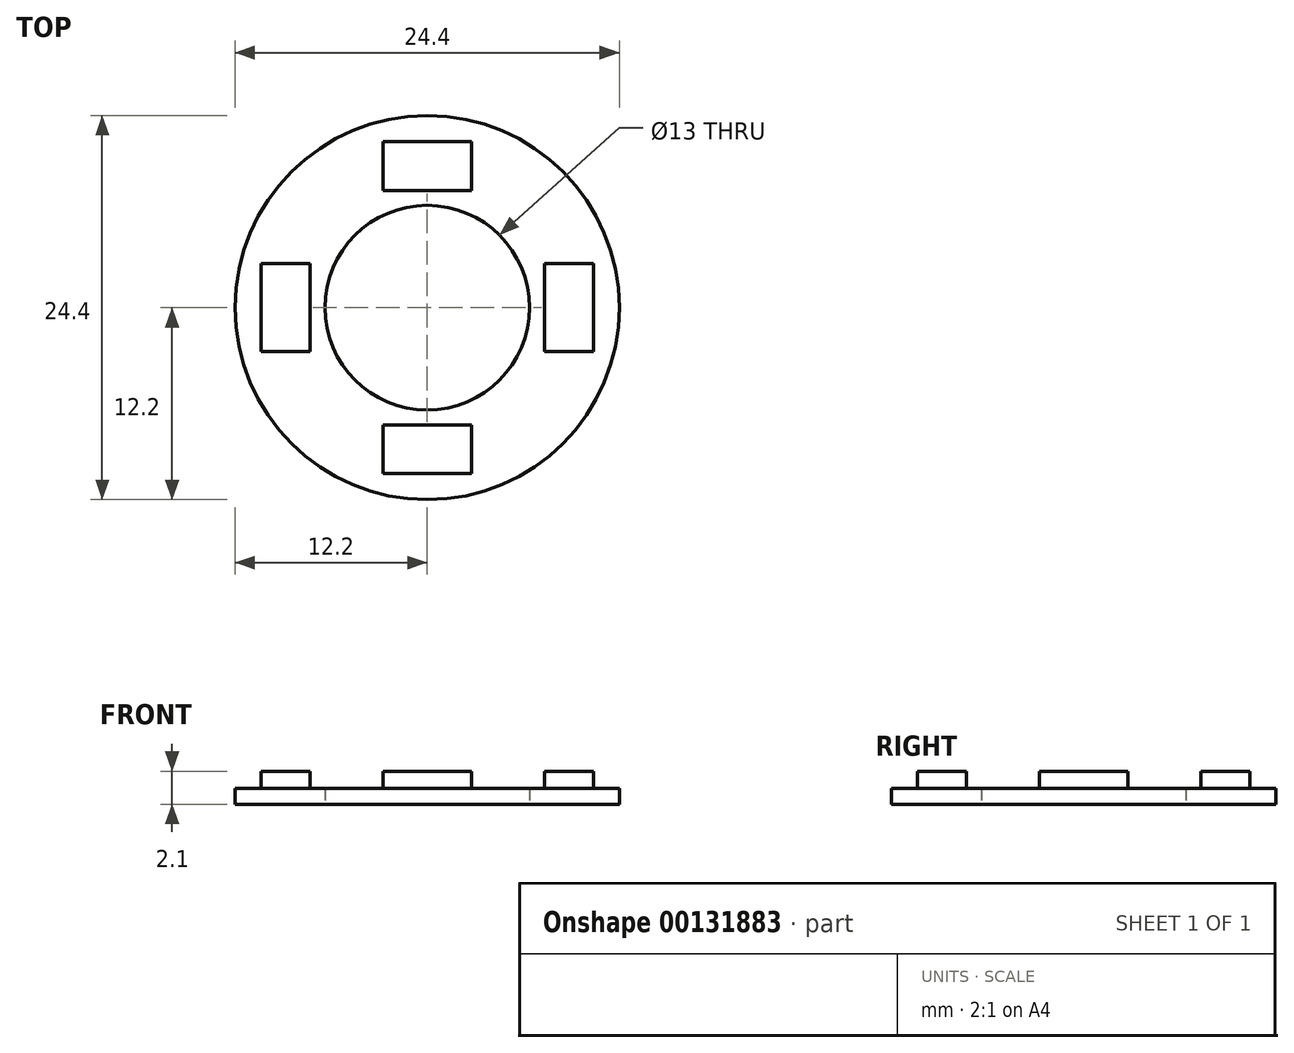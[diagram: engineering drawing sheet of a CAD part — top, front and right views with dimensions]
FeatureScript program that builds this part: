
annotation { "Feature Type Name" : "Feature", "Feature Type Description" : "" }
export const myFeature = defineFeature(function(context is Context, id is Id, definition is map)
    precondition{}
    {
        {
            var Q0;
            Q0=qCreatedBy(makeId("Top.planeOp"),FACE);
            var sketch = newSketch(context, id + "F0", { "sketchPlane" : qUnion([Q0])});
            skCircle(sketch, "E0", {"center": v(0, 0) * mm, "radius": 12.2 * mm});
            skCircle(sketch, "E1", {"center": v(0, 0) * mm, "radius": 6.5 * mm});
            skSolve(sketch);
        }
        {
            var Q0;
            Q0 = qSketchRegion(id + "F0", true);
            extrude(context, id + "F1", {"entities" : qUnion([Q0]), "depth" : 1 * mm});
        }
        {
            var Q0;
            Q0=qCreatedBy(makeId("Top.planeOp"),FACE);
            cPlane(context, id + "F2", {"entities" : qUnion([Q0]), "cplaneType" : CPlaneType.OFFSET, "offset" : 1 * mm, "width" : 150 * mm, "height" : 150 * mm});
        }
        {
            var Q0;
            Q0=qCreatedBy(id+"F2.planeOp",FACE);
            var sketch = newSketch(context, id + "F3", { "sketchPlane" : qUnion([Q0])});
            skLineSegment(sketch, "E2.bottom", {"start": v(2.8, 10.55) * mm, "end": v(-2.8, 10.55) * mm});
            skLineSegment(sketch, "E2.top", {"start": v(2.8, 7.45) * mm, "end": v(-2.8, 7.45) * mm});
            skLineSegment(sketch, "E2.left", {"start": v(2.8, 10.55) * mm, "end": v(2.8, 7.45) * mm});
            skLineSegment(sketch, "E2.right", {"start": v(-2.8, 10.55) * mm, "end": v(-2.8, 7.45) * mm});
            skPoint(sketch, "E2.middle", {"position": v(0, 9) * mm});
            skLineSegment(sketch, "E3", {"start": v(0, 0) * mm, "end": v(10.83, 10.83) * mm});
            skPoint(sketch, "E4.MirrorP", {"position": v(9, 0) * mm});
            skLineSegment(sketch, "E5.MirrorCS", {"start": v(10.55, 2.8) * mm, "end": v(10.55, -2.8) * mm});
            skLineSegment(sketch, "E6.MirrorCS", {"start": v(7.45, 2.8) * mm, "end": v(7.45, -2.8) * mm});
            skLineSegment(sketch, "E7.MirrorCS", {"start": v(10.55, -2.8) * mm, "end": v(7.45, -2.8) * mm});
            skLineSegment(sketch, "E8.MirrorCS", {"start": v(10.55, 2.8) * mm, "end": v(7.45, 2.8) * mm});
            skLineSegment(sketch, "E9.MirrorCS", {"start": v(2.8, -10.55) * mm, "end": v(-2.8, -10.55) * mm});
            skLineSegment(sketch, "E10.MirrorCS", {"start": v(2.8, -7.45) * mm, "end": v(-2.8, -7.45) * mm});
            skPoint(sketch, "E11.MirrorP", {"position": v(0, -9) * mm});
            skLineSegment(sketch, "E12.MirrorCS", {"start": v(2.8, -10.55) * mm, "end": v(2.8, -7.45) * mm});
            skLineSegment(sketch, "E13.MirrorCS", {"start": v(-2.8, -10.55) * mm, "end": v(-2.8, -7.45) * mm});
            skPoint(sketch, "E14.MirrorP", {"position": v(-9, 0) * mm});
            skLineSegment(sketch, "E15.MirrorCS", {"start": v(-10.55, 2.8) * mm, "end": v(-10.55, -2.8) * mm});
            skLineSegment(sketch, "E16.MirrorCS", {"start": v(-7.45, 2.8) * mm, "end": v(-7.45, -2.8) * mm});
            skLineSegment(sketch, "E17.MirrorCS", {"start": v(-10.55, 2.8) * mm, "end": v(-7.45, 2.8) * mm});
            skLineSegment(sketch, "E18.MirrorCS", {"start": v(-10.55, -2.8) * mm, "end": v(-7.45, -2.8) * mm});
            skSolve(sketch);
        }
        {
            var Q0;
            Q0 = qSketchRegion(id + "F3", true);
            extrude(context, id + "F4", {"entities" : qUnion([Q0]), "depth" : 1.1 * mm});
        }
    });
